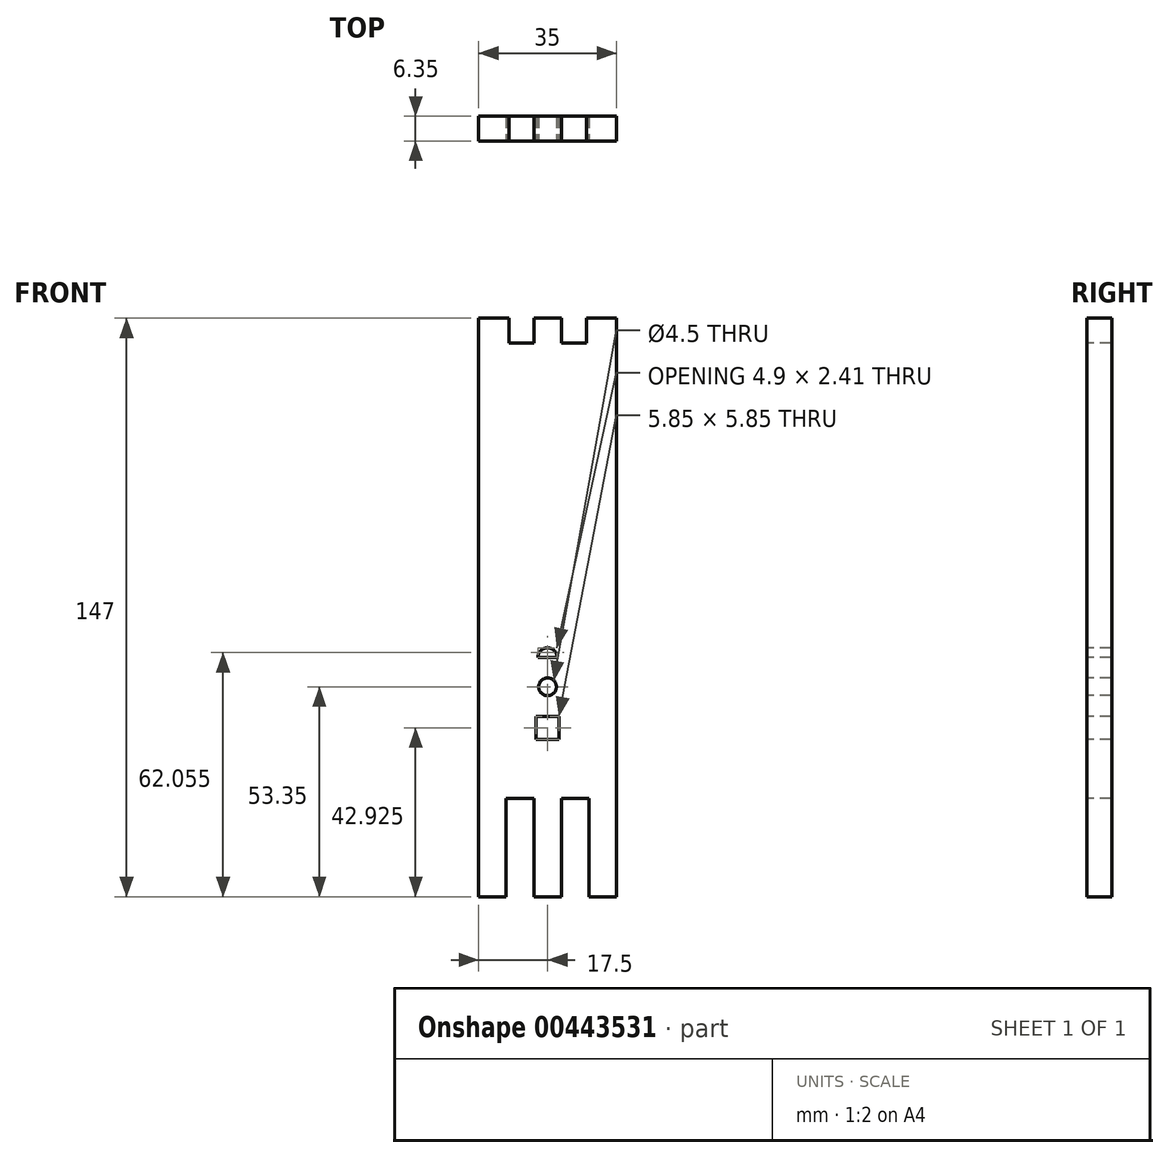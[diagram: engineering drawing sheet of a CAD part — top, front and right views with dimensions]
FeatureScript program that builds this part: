
annotation { "Feature Type Name" : "Feature", "Feature Type Description" : "" }
export const myFeature = defineFeature(function(context is Context, id is Id, definition is map)
    precondition{}
    {
        {
            var Q0;
            Q0=qCreatedBy(makeId("Front.planeOp"),FACE);
            var sketch = newSketch(context, id + "F0", { "sketchPlane" : qUnion([Q0])});
            skLineSegment(sketch, "E0.bottom", {"start": v(0, 0) * mm, "end": v(35, 0) * mm});
            skLineSegment(sketch, "E0.top", {"start": v(0, 122) * mm, "end": v(35, 122) * mm});
            skLineSegment(sketch, "E0.left", {"start": v(0, 0) * mm, "end": v(0, 122) * mm});
            skLineSegment(sketch, "E0.right", {"start": v(35, 0) * mm, "end": v(35, 122) * mm});
            skSolve(sketch);
        }
        {
            var Q0;
            Q0=qSketchRegion(id+"F0",true);
            extrude(context, id + "F1", {"entities" : qUnion([Q0]), "depth" : 6.35 * mm});
        }
        {
            var Q0;
            Q0=makeQuery(id+"F1.opExtrude","CAP_FACE",FACE,{"disambiguationData":[OSD([sQuery(id+"F0.wireOp",EDGE,"E0.bottom"),sQuery(id+"F0.wireOp",EDGE,"E0.top"),sQuery(id+"F0.wireOp",EDGE,"E0.left"),sQuery(id+"F0.wireOp",EDGE,"E0.right")])],"isStart":false});
            var sketch = newSketch(context, id + "F2", { "sketchPlane" : qUnion([Q0])});
            skLineSegment(sketch, "E1.bottom", {"start": v(0, 0) * mm, "end": v(7, 0) * mm});
            skLineSegment(sketch, "E1.top", {"start": v(0, -25) * mm, "end": v(7, -25) * mm});
            skLineSegment(sketch, "E1.left", {"start": v(0, 0) * mm, "end": v(0, -25) * mm});
            skLineSegment(sketch, "E1.right", {"start": v(7, 0) * mm, "end": v(7, -25) * mm});
            skLineSegment(sketch, "E2.bottom", {"start": v(28, 0) * mm, "end": v(35, 0) * mm});
            skLineSegment(sketch, "E2.top", {"start": v(28, -25) * mm, "end": v(35, -25) * mm});
            skLineSegment(sketch, "E2.left", {"start": v(28, 0) * mm, "end": v(28, -25) * mm});
            skLineSegment(sketch, "E2.right", {"start": v(35, 0) * mm, "end": v(35, -25) * mm});
            skLineSegment(sketch, "E3.bottom", {"start": v(14, 0) * mm, "end": v(21, 0) * mm});
            skLineSegment(sketch, "E3.top", {"start": v(14, -25) * mm, "end": v(21, -25) * mm});
            skLineSegment(sketch, "E3.left", {"start": v(14, 0) * mm, "end": v(14, -25) * mm});
            skLineSegment(sketch, "E3.right", {"start": v(21, 0) * mm, "end": v(21, -25) * mm});
            skSolve(sketch);
        }
        {
            var Q0;
            Q0=qSketchRegion(id+"F2",true);
            extrude(context, id + "F3", {"entities" : qUnion([Q0]), "operationType" : NewBodyOperationType.ADD, "oppositeDirection" : true, "depth" : 6.35 * mm});
        }
        {
            var Q0;
            Q0=makeQuery(id+"F1.opExtrude","CAP_FACE",FACE,{"disambiguationData":[OSD([sQuery(id+"F0.wireOp",EDGE,"E0.bottom"),sQuery(id+"F0.wireOp",EDGE,"E0.top"),sQuery(id+"F0.wireOp",EDGE,"E0.left"),sQuery(id+"F0.wireOp",EDGE,"E0.right")])],"isStart":false});
            var sketch = newSketch(context, id + "F4", { "sketchPlane" : qUnion([Q0])});
            skLineSegment(sketch, "E4.bottom", {"start": v(14.58, 20.85) * mm, "end": v(20.43, 20.85) * mm});
            skLineSegment(sketch, "E4.top", {"start": v(14.58, 15) * mm, "end": v(20.43, 15) * mm});
            skLineSegment(sketch, "E4.left", {"start": v(14.58, 20.85) * mm, "end": v(14.58, 15) * mm});
            skLineSegment(sketch, "E4.right", {"start": v(20.43, 20.85) * mm, "end": v(20.43, 15) * mm});
            skPoint(sketch, "E5", {"position": v(17.5, 15) * mm});
            skPoint(sketch, "E6", {"position": v(0, 15) * mm});
            skPoint(sketch, "E7", {"position": v(35, 15) * mm});
            skSolve(sketch);
        }
        {
            var Q0;
            Q0=qSketchRegion(id+"F4",true);
            extrude(context, id + "F5", {"entities" : qUnion([Q0]), "operationType" : NewBodyOperationType.REMOVE, "oppositeDirection" : true, "depth" : 25 * mm});
        }
        {
            var Q0;
            Q0=makeQuery(id+"F3.boolean.opBoolean","MERGE",FACE,{"derivedFrom":[makeQuery(id+"F1.opExtrude","CAP_FACE",FACE,{"disambiguationData":[OSD([sQuery(id+"F0.wireOp",EDGE,"E0.bottom"),sQuery(id+"F0.wireOp",EDGE,"E0.top"),sQuery(id+"F0.wireOp",EDGE,"E0.left"),sQuery(id+"F0.wireOp",EDGE,"E0.right")])],"isStart":false}),makeQuery(id+"F3.opExtrude","CAP_FACE",FACE,{"disambiguationData":[OSD([sQuery(id+"F2.wireOp",EDGE,"E1.bottom"),sQuery(id+"F2.wireOp",EDGE,"E1.top"),sQuery(id+"F2.wireOp",EDGE,"E1.left"),sQuery(id+"F2.wireOp",EDGE,"E1.right")])],"isStart":true}),makeQuery(id+"F3.opExtrude","CAP_FACE",FACE,{"disambiguationData":[OSD([sQuery(id+"F2.wireOp",EDGE,"E2.bottom"),sQuery(id+"F2.wireOp",EDGE,"E2.top"),sQuery(id+"F2.wireOp",EDGE,"E2.left"),sQuery(id+"F2.wireOp",EDGE,"E2.right")])],"isStart":true}),makeQuery(id+"F3.opExtrude","CAP_FACE",FACE,{"disambiguationData":[OSD([sQuery(id+"F2.wireOp",EDGE,"E3.bottom"),sQuery(id+"F2.wireOp",EDGE,"E3.top"),sQuery(id+"F2.wireOp",EDGE,"E3.left"),sQuery(id+"F2.wireOp",EDGE,"E3.right")])],"isStart":true})]});
            var sketch = newSketch(context, id + "F6", { "sketchPlane" : qUnion([Q0])});
            skCircle(sketch, "E8", {"center": v(17.5, 28.35) * mm, "radius": 2.25 * mm});
            skPoint(sketch, "E8.centerSnap0", {"position": v(17.5, 20.85) * mm});
            skLineSegment(sketch, "E9", {"start": v(15.05, 35.85) * mm, "end": v(19.95, 35.85) * mm});
            skPoint(sketch, "E10.endSnap0", {"position": v(17.5, 35.85) * mm});
            skArc(sketch, "E11", {"start": v(19.95, 35.85) * mm, "mid": v(17.5, 38.26) * mm, "end": v(15.05, 35.85) * mm});
            skSolve(sketch);
        }
        {
            var Q0;
            Q0=qSketchRegion(id+"F6",true);
            extrude(context, id + "F7", {"entities" : qUnion([Q0]), "operationType" : NewBodyOperationType.REMOVE, "oppositeDirection" : true, "depth" : 25 * mm});
        }
        {
            var Q0;
            Q0=makeQuery(id+"F3.boolean.opBoolean","MERGE",FACE,{"derivedFrom":[makeQuery(id+"F1.opExtrude","CAP_FACE",FACE,{"disambiguationData":[OSD([sQuery(id+"F0.wireOp",EDGE,"E0.bottom"),sQuery(id+"F0.wireOp",EDGE,"E0.top"),sQuery(id+"F0.wireOp",EDGE,"E0.left"),sQuery(id+"F0.wireOp",EDGE,"E0.right")])],"isStart":false}),makeQuery(id+"F3.opExtrude","CAP_FACE",FACE,{"disambiguationData":[OSD([sQuery(id+"F2.wireOp",EDGE,"E1.bottom"),sQuery(id+"F2.wireOp",EDGE,"E1.top"),sQuery(id+"F2.wireOp",EDGE,"E1.left"),sQuery(id+"F2.wireOp",EDGE,"E1.right")])],"isStart":true}),makeQuery(id+"F3.opExtrude","CAP_FACE",FACE,{"disambiguationData":[OSD([sQuery(id+"F2.wireOp",EDGE,"E2.bottom"),sQuery(id+"F2.wireOp",EDGE,"E2.top"),sQuery(id+"F2.wireOp",EDGE,"E2.left"),sQuery(id+"F2.wireOp",EDGE,"E2.right")])],"isStart":true}),makeQuery(id+"F3.opExtrude","CAP_FACE",FACE,{"disambiguationData":[OSD([sQuery(id+"F2.wireOp",EDGE,"E3.bottom"),sQuery(id+"F2.wireOp",EDGE,"E3.top"),sQuery(id+"F2.wireOp",EDGE,"E3.left"),sQuery(id+"F2.wireOp",EDGE,"E3.right")])],"isStart":true})]});
            var sketch = newSketch(context, id + "F8", { "sketchPlane" : qUnion([Q0])});
            skLineSegment(sketch, "E12.bottom", {"start": v(7.65, 122) * mm, "end": v(14, 122) * mm});
            skLineSegment(sketch, "E12.top", {"start": v(7.65, 115.65) * mm, "end": v(14, 115.65) * mm});
            skLineSegment(sketch, "E12.left", {"start": v(7.65, 122) * mm, "end": v(7.65, 115.65) * mm});
            skLineSegment(sketch, "E12.right", {"start": v(14, 122) * mm, "end": v(14, 115.65) * mm});
            skLineSegment(sketch, "E13.bottom", {"start": v(21, 122) * mm, "end": v(27.35, 122) * mm});
            skLineSegment(sketch, "E13.top", {"start": v(21, 115.65) * mm, "end": v(27.35, 115.65) * mm});
            skLineSegment(sketch, "E13.left", {"start": v(21, 122) * mm, "end": v(21, 115.65) * mm});
            skLineSegment(sketch, "E13.right", {"start": v(27.35, 122) * mm, "end": v(27.35, 115.65) * mm});
            skSolve(sketch);
        }
        {
            var Q0;
            Q0=qSketchRegion(id+"F8",true);
            extrude(context, id + "F9", {"entities" : qUnion([Q0]), "operationType" : NewBodyOperationType.REMOVE, "oppositeDirection" : true, "depth" : 25 * mm});
        }
    });
